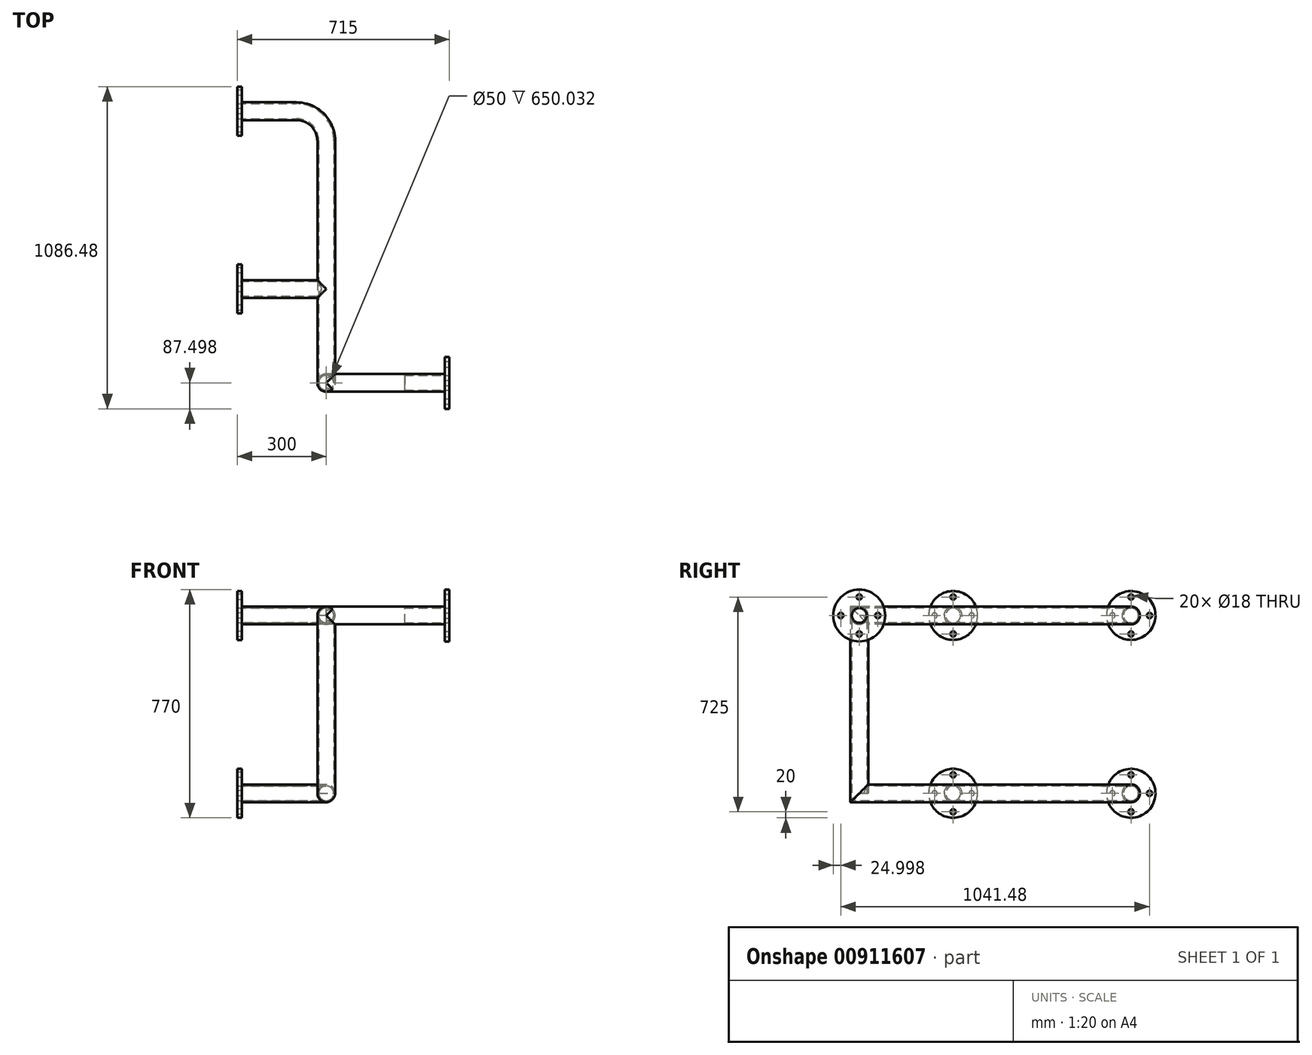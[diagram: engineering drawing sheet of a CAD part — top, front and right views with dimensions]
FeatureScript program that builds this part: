
annotation { "Feature Type Name" : "Feature", "Feature Type Description" : "" }
export const myFeature = defineFeature(function(context is Context, id is Id, definition is map)
    precondition{}
    {
        {
            var Q0;
            Q0=qCreatedBy(makeId("Top.planeOp"),FACE);
            var sketch = newSketch(context, id + "F0", { "sketchPlane" : qUnion([Q0])});
            skLineSegment(sketch, "E0.bottom", {"start": v(0, 0) * mm, "end": v(200, 0) * mm});
            skLineSegment(sketch, "E0.top", {"start": v(0, -600) * mm, "end": v(300, -600) * mm});
            skLineSegment(sketch, "E0.right", {"start": v(300, -100) * mm, "end": v(300, -600) * mm});
            skLineSegment(sketch, "E1", {"start": v(300, -600) * mm, "end": v(300, -916.48) * mm});
            skPoint(sketch, "E2.visualSharp", {"position": v(300, 0) * mm});
            skArc(sketch, "E2.filletArc", {"start": v(300, -100) * mm, "mid": v(270.71, -29.29) * mm, "end": v(200, 0) * mm});
            skSolve(sketch);
        }
        {
            var Q0;
            Q0=qCreatedBy(makeId("Top.planeOp"),FACE);
            cPlane(context, id + "F1", {"entities" : qUnion([Q0]), "cplaneType" : CPlaneType.OFFSET, "offset" : 600 * mm, "width" : 150 * mm, "height" : 150 * mm});
        }
        {
            var Q0;
            Q0=qCreatedBy(makeId("Right.planeOp"),FACE);
            cPlane(context, id + "F2", {"entities" : qUnion([Q0]), "cplaneType" : CPlaneType.OFFSET, "offset" : 300 * mm, "width" : 150 * mm, "height" : 150 * mm});
        }
        {
            var Q0;
            Q0=qCreatedBy(id+"F1.planeOp",FACE);
            var sketch = newSketch(context, id + "F3", { "sketchPlane" : qUnion([Q0])});
            skLineSegment(sketch, "E3.0", {"start": v(0, 0) * mm, "end": v(200, 0) * mm});
            skLineSegment(sketch, "E3.1", {"start": v(300, -100) * mm, "end": v(300, -600) * mm});
            skLineSegment(sketch, "E3.2", {"start": v(0, -600) * mm, "end": v(300, -600) * mm});
            skLineSegment(sketch, "E3.3", {"start": v(300, -600) * mm, "end": v(300, -916.48) * mm});
            skArc(sketch, "E3.4", {"start": v(300, -100) * mm, "mid": v(270.71, -29.29) * mm, "end": v(200, 0) * mm});
            skSolve(sketch);
        }
        {
            var Q0;
            Q0=qCreatedBy(makeId("Right.planeOp"),FACE);
            var sketch = newSketch(context, id + "F4", { "sketchPlane" : qUnion([Q0])});
            skCircle(sketch, "E4", {"center": v(0, 0) * mm, "radius": 25 * mm});
            skCircle(sketch, "E5", {"center": v(0, 0) * mm, "radius": 30 * mm});
            skCircle(sketch, "E6.0.1.0", {"center": v(0, 600) * mm, "radius": 30 * mm});
            skCircle(sketch, "E6.0.1.1", {"center": v(0, 600) * mm, "radius": 25 * mm});
            skCircle(sketch, "E6.1.0.0", {"center": v(-600, 0) * mm, "radius": 30 * mm});
            skCircle(sketch, "E6.1.0.1", {"center": v(-600, 0) * mm, "radius": 25 * mm});
            skCircle(sketch, "E6.1.1.0", {"center": v(-600, 600) * mm, "radius": 30 * mm});
            skCircle(sketch, "E6.1.1.1", {"center": v(-600, 600) * mm, "radius": 25 * mm});
            skLineSegment(sketch, "E6.direction1", {"start": v(0, 0) * mm, "end": v(-600, 0) * mm, "construction": true});
            skLineSegment(sketch, "E6.direction2", {"start": v(0, 0) * mm, "end": v(0, 600) * mm, "construction": true});
            skSolve(sketch);
        }
        {
            var Q0;
            Q0=makeQuery(id+"F4.imprint","IMPRINT",FACE,{"disambiguationData":[TD([[makeQuery(id+"F4.imprint","IMPRINT",EDGE,{"derivedFrom":sQuery(id+"F4.wireOp",EDGE,"E6.0.1.0")}),1.0]])]});
            var sketch = newSketch(context, id + "F5", { "sketchPlane" : qUnion([Q0])});
            skPoint(sketch, "E7.0", {"position": v(0, 600) * mm});
            skCircle(sketch, "E8", {"center": v(0, 600) * mm, "radius": 82.5 * mm});
            skCircle(sketch, "E9", {"center": v(0, 662.5) * mm, "radius": 9 * mm});
            skCircle(sketch, "E10.1.0", {"center": v(-62.5, 600) * mm, "radius": 9 * mm});
            skCircle(sketch, "E10.2.0", {"center": v(0, 537.5) * mm, "radius": 9 * mm});
            skCircle(sketch, "E10.3.0", {"center": v(62.5, 600) * mm, "radius": 9 * mm});
            skCircle(sketch, "E11.0.0", {"center": v(0, 600) * mm, "radius": 25 * mm});
            skCircle(sketch, "E12.0.1.0", {"center": v(0, -62.5) * mm, "radius": 9 * mm});
            skCircle(sketch, "E12.0.1.1", {"center": v(-62.5, 0) * mm, "radius": 9 * mm});
            skCircle(sketch, "E12.0.1.2", {"center": v(0, 0) * mm, "radius": 82.5 * mm});
            skCircle(sketch, "E12.0.1.3", {"center": v(62.5, 0) * mm, "radius": 9 * mm});
            skPoint(sketch, "E12.0.1.4", {"position": v(0, 0) * mm});
            skCircle(sketch, "E12.0.1.5", {"center": v(0, 62.5) * mm, "radius": 9 * mm});
            skCircle(sketch, "E12.0.1.6", {"center": v(0, 0) * mm, "radius": 25 * mm});
            skPoint(sketch, "E12.0.1.7", {"position": v(0, 0) * mm});
            skCircle(sketch, "E12.1.0.0", {"center": v(-600, 537.5) * mm, "radius": 9 * mm});
            skCircle(sketch, "E12.1.0.1", {"center": v(-662.5, 600) * mm, "radius": 9 * mm});
            skCircle(sketch, "E12.1.0.2", {"center": v(-600, 600) * mm, "radius": 82.5 * mm});
            skCircle(sketch, "E12.1.0.3", {"center": v(-537.5, 600) * mm, "radius": 9 * mm});
            skPoint(sketch, "E12.1.0.4", {"position": v(-600, 600) * mm});
            skCircle(sketch, "E12.1.0.5", {"center": v(-600, 662.5) * mm, "radius": 9 * mm});
            skCircle(sketch, "E12.1.0.6", {"center": v(-600, 600) * mm, "radius": 25 * mm});
            skPoint(sketch, "E12.1.0.7", {"position": v(-600, 600) * mm});
            skCircle(sketch, "E12.1.1.0", {"center": v(-600, -62.5) * mm, "radius": 9 * mm});
            skCircle(sketch, "E12.1.1.1", {"center": v(-662.5, 0) * mm, "radius": 9 * mm});
            skCircle(sketch, "E12.1.1.2", {"center": v(-600, 0) * mm, "radius": 82.5 * mm});
            skCircle(sketch, "E12.1.1.3", {"center": v(-537.5, 0) * mm, "radius": 9 * mm});
            skPoint(sketch, "E12.1.1.4", {"position": v(-600, 0) * mm});
            skCircle(sketch, "E12.1.1.5", {"center": v(-600, 62.5) * mm, "radius": 9 * mm});
            skCircle(sketch, "E12.1.1.6", {"center": v(-600, 0) * mm, "radius": 25 * mm});
            skPoint(sketch, "E12.1.1.7", {"position": v(-600, 0) * mm});
            skLineSegment(sketch, "E12.direction1", {"start": v(0, 537.5) * mm, "end": v(-600, 537.5) * mm, "construction": true});
            skLineSegment(sketch, "E12.direction2", {"start": v(0, 537.5) * mm, "end": v(0, -62.5) * mm, "construction": true});
            skSolve(sketch);
        }
        {
            var Q0;
            Q0=qCreatedBy(id+"F2.planeOp",FACE);
            var sketch = newSketch(context, id + "F6", { "sketchPlane" : qUnion([Q0])});
            skLineSegment(sketch, "E13.0", {"start": v(-600, 600) * mm, "end": v(-916.48, 600) * mm});
            skLineSegment(sketch, "E14.0", {"start": v(-600, 0) * mm, "end": v(-916.48, 0) * mm});
            skLineSegment(sketch, "E15", {"start": v(-916.48, 600) * mm, "end": v(-916.48, 0) * mm});
            skSolve(sketch);
        }
        {
            var Q0;
            Q0=makeQuery(id+"F4.imprint","IMPRINT",FACE,{"disambiguationData":[TD([[makeQuery(id+"F4.imprint","IMPRINT",EDGE,{"derivedFrom":sQuery(id+"F4.wireOp",EDGE,"E6.0.1.0")}),1.0]])]});
            var Q1;
            Q1=sQuery(id+"F3.wireOp",EDGE,"E3.0");
            var Q2;
            Q2=sQuery(id+"F3.wireOp",EDGE,"E3.4");
            var Q3;
            Q3=sQuery(id+"F3.wireOp",EDGE,"E3.1");
            var Q4;
            Q4=sQuery(id+"F3.wireOp",EDGE,"E3.3");
            var Q5;
            Q5=sQuery(id+"F6.wireOp",EDGE,"E15");
            sweep(context, id + "F7", {"profiles" : qUnion([Q0]), "path" : qUnion([Q1, Q2, Q3, Q4, Q5])});
        }
        {
            var Q0;
            Q0=makeQuery(id+"F4.imprint","IMPRINT",FACE,{"disambiguationData":[TD([[makeQuery(id+"F4.imprint","IMPRINT",EDGE,{"derivedFrom":sQuery(id+"F4.wireOp",EDGE,"E4")}),-1.0]])]});
            var Q1;
            Q1=sQuery(id+"F0.wireOp",EDGE,"E0.bottom");
            var Q2;
            Q2=sQuery(id+"F0.wireOp",EDGE,"E2.filletArc");
            var Q3;
            Q3=sQuery(id+"F0.wireOp",EDGE,"E0.right");
            var Q4;
            Q4=sQuery(id+"F0.wireOp",EDGE,"E1");
            var Q5;
            Q5=sQuery(id+"F6.wireOp",EDGE,"E15");
            sweep(context, id + "F8", {"operationType" : NewBodyOperationType.ADD, "profiles" : qUnion([Q0]), "path" : qUnion([Q1, Q2, Q3, Q4, Q5])});
        }
        {
            var Q0;
            Q0=makeQuery(id+"F4.imprint","IMPRINT",FACE,{"disambiguationData":[TD([[makeQuery(id+"F4.imprint","IMPRINT",EDGE,{"derivedFrom":sQuery(id+"F4.wireOp",EDGE,"E6.1.1.0")}),1.0]])]});
            extrude(context, id + "F9", {"entities" : qUnion([Q0]), "operationType" : NewBodyOperationType.ADD, "endBound" : BoundingType.UP_TO_NEXT, "depth" : 25 * mm, "offsetDistance" : 25 * mm});
        }
        {
            var Q0;
            Q0=makeQuery(id+"F4.imprint","IMPRINT",FACE,{"disambiguationData":[TD([[makeQuery(id+"F4.imprint","IMPRINT",EDGE,{"derivedFrom":sQuery(id+"F4.wireOp",EDGE,"E6.1.0.0")}),1.0]])]});
            extrude(context, id + "F10", {"entities" : qUnion([Q0]), "operationType" : NewBodyOperationType.ADD, "endBound" : BoundingType.UP_TO_NEXT, "depth" : 25 * mm, "offsetDistance" : 25 * mm});
        }
        {
            var Q0;
            Q0=qSketchRegion(id+"F5",true);
            extrude(context, id + "F11", {"entities" : qUnion([Q0]), "operationType" : NewBodyOperationType.ADD, "depth" : 15 * mm, "offsetDistance" : 25 * mm});
        }
        {
            var Q0;
            Q0=qCreatedBy(makeId("Front.planeOp"),FACE);
            cPlane(context, id + "F12", {"entities" : qUnion([Q0]), "cplaneType" : CPlaneType.OFFSET, "offset" : (920 - 3.52) * mm, "width" : 150 * mm, "height" : 150 * mm});
        }
        {
            var Q0;
            Q0=qCreatedBy(id+"F12.planeOp",FACE);
            var sketch = newSketch(context, id + "F13", { "sketchPlane" : qUnion([Q0])});
            skPoint(sketch, "E16.0", {"position": v(300, 600) * mm});
            skLineSegment(sketch, "E17", {"start": v(300, 600) * mm, "end": v(500, 600) * mm});
            skSolve(sketch);
        }
        {
            var Q0;
            Q0=qCreatedBy(id+"F2.planeOp",FACE);
            var sketch = newSketch(context, id + "F14", { "sketchPlane" : qUnion([Q0])});
            skPoint(sketch, "E18.0", {"position": v(-916.48, 600) * mm});
            skCircle(sketch, "E19", {"center": v(-916.48, 600) * mm, "radius": 30 * mm});
            skSolve(sketch);
        }
        {
            var Q0;
            Q0=qSketchRegion(id+"F14",true);
            extrude(context, id + "F15", {"entities" : qUnion([Q0]), "operationType" : NewBodyOperationType.ADD, "depth" : 415 * mm, "offsetDistance" : 25 * mm});
        }
        {
            var Q0;
            Q0=makeQuery(id+"F15.opExtrude","CAP_FACE",FACE,{"disambiguationData":[OSD([sQuery(id+"F14.wireOp",EDGE,"E19")])],"isStart":false});
            var sketch = newSketch(context, id + "F16", { "sketchPlane" : qUnion([Q0])});
            skCircle(sketch, "E20", {"center": v(-916.48, 600) * mm, "radius": 87.5 * mm});
            skCircle(sketch, "E21", {"center": v(-916.48, 537.5) * mm, "radius": 9 * mm});
            skCircle(sketch, "E22", {"center": v(-916.48, 600) * mm, "radius": 25 * mm});
            skCircle(sketch, "E23.1.0", {"center": v(-853.98, 600) * mm, "radius": 9 * mm});
            skCircle(sketch, "E23.2.0", {"center": v(-916.48, 662.5) * mm, "radius": 9 * mm});
            skCircle(sketch, "E23.3.0", {"center": v(-978.98, 600) * mm, "radius": 9 * mm});
            skCircle(sketch, "E24.0", {"center": v(-916.48, 600) * mm, "radius": 30 * mm});
            skSolve(sketch);
        }
        {
            var Q0;
            Q0=makeQuery(id+"F16.imprint","IMPRINT",FACE,{"disambiguationData":[TD([[makeQuery(id+"F16.imprint","IMPRINT",EDGE,{"derivedFrom":sQuery(id+"F16.wireOp",EDGE,"E20")}),1.0]])]});
            extrude(context, id + "F17", {"entities" : qUnion([Q0]), "operationType" : NewBodyOperationType.ADD, "oppositeDirection" : true, "depth" : 15 * mm, "offsetDistance" : 25 * mm});
        }
        {
            var Q0;
            Q0=makeQuery(id+"F16.imprint","IMPRINT",FACE,{"disambiguationData":[TD([[makeQuery(id+"F16.imprint","IMPRINT",EDGE,{"derivedFrom":sQuery(id+"F16.wireOp",EDGE,"E22")}),1.0]])]});
            extrude(context, id + "F18", {"entities" : qUnion([Q0]), "operationType" : NewBodyOperationType.REMOVE, "oppositeDirection" : true, "depth" : 150 * mm, "offsetDistance" : 25 * mm});
        }
    });
